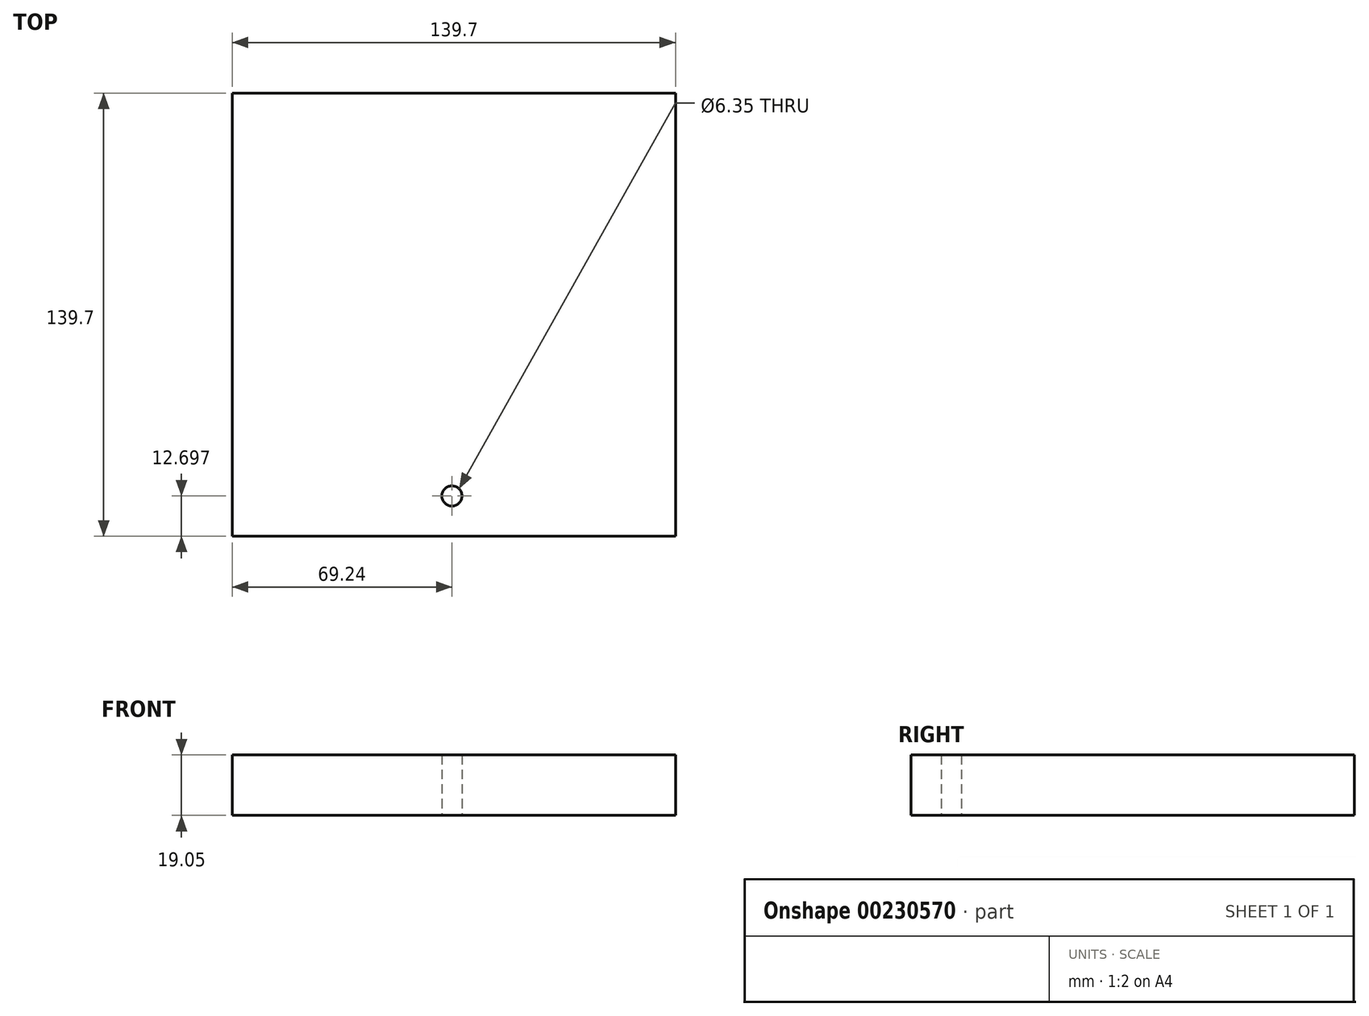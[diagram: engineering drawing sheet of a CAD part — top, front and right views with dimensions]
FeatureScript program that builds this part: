
annotation { "Feature Type Name" : "Feature", "Feature Type Description" : "" }
export const myFeature = defineFeature(function(context is Context, id is Id, definition is map)
    precondition{}
    {
        {
            var Q0;
            Q0=qCreatedBy(makeId("Top.planeOp"),FACE);
            var sketch = newSketch(context, id + "F0", { "sketchPlane" : qUnion([Q0])});
            skLineSegment(sketch, "E0.bottom", {"start": v(70.46, 70.3) * mm, "end": v(-69.24, 70.3) * mm});
            skLineSegment(sketch, "E0.top", {"start": v(70.46, -69.4) * mm, "end": v(-69.24, -69.4) * mm});
            skLineSegment(sketch, "E0.left", {"start": v(70.46, 70.3) * mm, "end": v(70.46, -69.4) * mm});
            skLineSegment(sketch, "E0.right", {"start": v(-69.24, 70.3) * mm, "end": v(-69.24, -69.4) * mm});
            skPoint(sketch, "E0.middle", {"position": v(0.6, 0.46) * mm});
            skLineSegment(sketch, "E1", {"start": v(0, -69.4) * mm, "end": v(0, -56.7) * mm});
            skCircle(sketch, "E2", {"center": v(0, -56.7) * mm, "radius": 3.18 * mm});
            skSolve(sketch);
        }
        {
            var Q0;
            Q0 = qSketchRegion(id + "F0", true);
            extrude(context, id + "F1", {"entities" : qUnion([Q0]), "depth" : 19.05 * mm});
        }
    });
